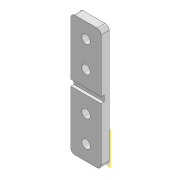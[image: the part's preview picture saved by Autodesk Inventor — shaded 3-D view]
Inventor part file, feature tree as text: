
AUTODESK INVENTOR PART (.ipt)
format: ipt  version: 2020 (Build 240168000, 168)  size: 139,776 bytes
history: native  units: mm
features: other x8, extrude x3, sketch x3, fillet x1
ambient origin geometry x8: Origin, YZ Plane, XZ Plane, XY Plane, X Axis, Y Axis, Z Axis, Center Point
bodies: Body1 (feature_tree)
feature tree (15):
  other  "Sólido1"
  other  "Plano de trabalho1"
  extrude  "Extrusão1"  Depth=4.0mm
  extrude  "Extrusão2"  Depth=3.0mm
  extrude  "Extrusão3"  Depth=1.5mm
  fillet  "Arredondamento1"  Radius=8.0mm
  sketch  "Esboço1"  dims[d0=4.0mm d1=0.0mm d4=28.5mm]
  other  "Referência1"
  other  "Referência2"
  sketch  "Esboço2"  dims[d5=28.5mm d6=3.0mm]
  sketch  "Esboço3"  dims[d7=4.2mm d8=4.2mm d9=8.0mm d10=8.0mm d11=1.5mm d12=0.0mm d13=10.0mm d14=0.0mm d15=1.5mm]
  other  "<userpath>\OneDrive\Área de Trabalho\Calorimetro 2022\Inventor\Montagem_suporte_termopar.iam"
  other  "Montagem_suporte_termopar.iam"
  other  "suporte_termopar:1"
  other  "Montagem1"
